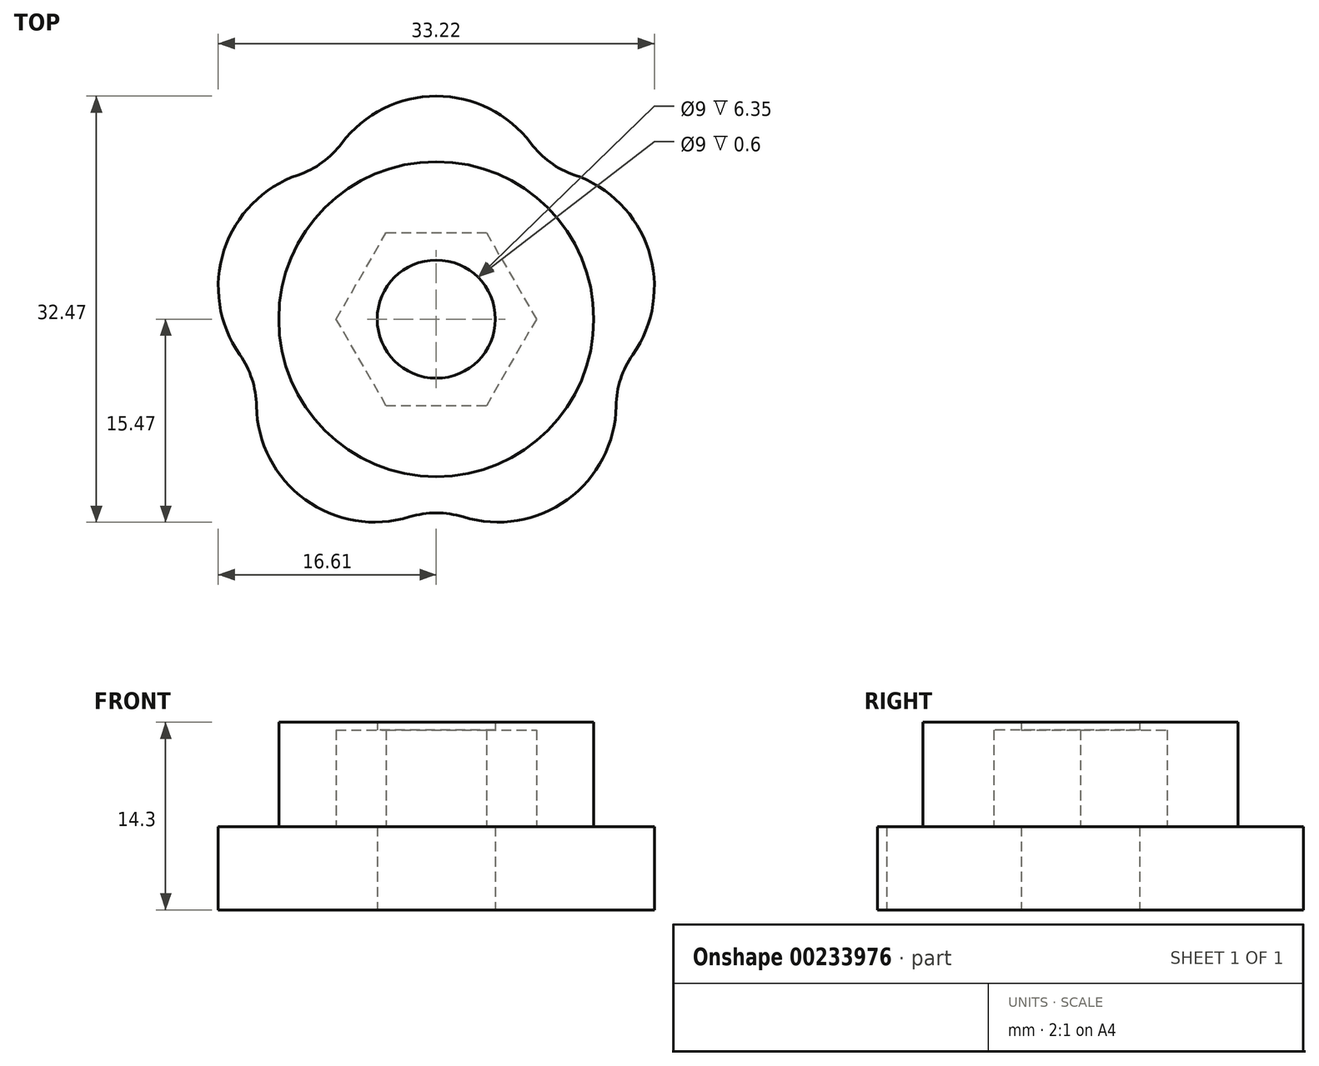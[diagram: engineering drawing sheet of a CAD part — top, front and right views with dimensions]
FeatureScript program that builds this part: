
annotation { "Feature Type Name" : "Feature", "Feature Type Description" : "" }
export const myFeature = defineFeature(function(context is Context, id is Id, definition is map)
    precondition{}
    {
        {
            var Q0;
            Q0=qCreatedBy(makeId("Top.planeOp"),FACE);
            var sketch = newSketch(context, id + "F0", { "sketchPlane" : qUnion([Q0])});
            skCircle(sketch, "E0", {"center": v(0, 0) * mm, "radius": 4.5 * mm});
            skArc(sketch, "E1", {"start": v(7.2, 13.4) * mm, "mid": v(0, 17) * mm, "end": v(-7.2, 13.4) * mm});
            skCircle(sketch, "E2", {"center": v(0, 0) * mm, "radius": 17 * mm, "construction": true});
            skArc(sketch, "E3.1.0", {"start": v(-10.53, 10.99) * mm, "mid": v(-16.17, 5.25) * mm, "end": v(-14.97, -2.7) * mm});
            skArc(sketch, "E3.2.0", {"start": v(-13.7, -6.61) * mm, "mid": v(-10, -13.75) * mm, "end": v(-2.06, -15.07) * mm});
            skArc(sketch, "E3.3.0", {"start": v(2.06, -15.07) * mm, "mid": v(10, -13.75) * mm, "end": v(13.7, -6.61) * mm});
            skArc(sketch, "E3.4.0", {"start": v(14.97, -2.7) * mm, "mid": v(16.17, 5.25) * mm, "end": v(10.53, 10.99) * mm});
            skLineSegment(sketch, "E4", {"start": v(0, 0) * mm, "end": v(-10, 13.75) * mm, "construction": true});
            skArc(sketch, "E5", {"start": v(-10.53, 10.99) * mm, "mid": v(-8.68, 11.95) * mm, "end": v(-7.2, 13.4) * mm});
            skArc(sketch, "E6.1.0", {"start": v(-13.7, -6.61) * mm, "mid": v(-14.04, -4.56) * mm, "end": v(-14.97, -2.7) * mm});
            skArc(sketch, "E6.2.0", {"start": v(2.06, -15.07) * mm, "mid": v(0, -14.77) * mm, "end": v(-2.06, -15.07) * mm});
            skArc(sketch, "E6.3.0", {"start": v(14.97, -2.7) * mm, "mid": v(14.04, -4.56) * mm, "end": v(13.7, -6.61) * mm});
            skArc(sketch, "E6.4.0", {"start": v(7.2, 13.4) * mm, "mid": v(8.68, 11.95) * mm, "end": v(10.53, 10.99) * mm});
            skSolve(sketch);
        }
        {
            var Q0;
            Q0=makeQuery(id+"F0.imprint","IMPRINT",FACE,{"disambiguationData":[TD([[makeQuery(id+"F0.imprint","IMPRINT",EDGE,{"derivedFrom":sQuery(id+"F0.wireOp",EDGE,"E0")}),-1.0]])]});
            extrude(context, id + "F1", {"entities" : qUnion([Q0]), "depth" : 6.35 * mm});
        }
        {
            var Q0;
            Q0=makeQuery(id+"F1.opExtrude","CAP_FACE",FACE,{"disambiguationData":[OSD([sQuery(id+"F0.wireOp",EDGE,"E0"),sQuery(id+"F0.wireOp",EDGE,"E1"),sQuery(id+"F0.wireOp",EDGE,"E3.1.0"),sQuery(id+"F0.wireOp",EDGE,"E3.2.0"),sQuery(id+"F0.wireOp",EDGE,"E3.3.0"),sQuery(id+"F0.wireOp",EDGE,"E3.4.0"),sQuery(id+"F0.wireOp",EDGE,"E5"),sQuery(id+"F0.wireOp",EDGE,"E6.1.0"),sQuery(id+"F0.wireOp",EDGE,"E6.2.0"),sQuery(id+"F0.wireOp",EDGE,"E6.3.0"),sQuery(id+"F0.wireOp",EDGE,"E6.4.0")])],"isStart":false});
            var sketch = newSketch(context, id + "F2", { "sketchPlane" : qUnion([Q0])});
            skCircle(sketch, "E7", {"center": v(0, 0) * mm, "radius": 12 * mm});
            skCircle(sketch, "E8.cCircle", {"center": v(0, 0) * mm, "radius": 6.6 * mm, "construction": true});
            skLineSegment(sketch, "E8.0", {"start": v(-3.81, 6.6) * mm, "end": v(3.81, 6.6) * mm});
            skLineSegment(sketch, "E8.1", {"start": v(3.81, 6.6) * mm, "end": v(7.62, 0) * mm});
            skLineSegment(sketch, "E8.2", {"start": v(7.62, 0) * mm, "end": v(3.81, -6.6) * mm});
            skLineSegment(sketch, "E8.3", {"start": v(3.81, -6.6) * mm, "end": v(-3.81, -6.6) * mm});
            skLineSegment(sketch, "E8.4", {"start": v(-3.81, -6.6) * mm, "end": v(-7.62, 0) * mm});
            skLineSegment(sketch, "E8.5", {"start": v(-7.62, 0) * mm, "end": v(-3.81, 6.6) * mm});
            skPoint(sketch, "E8.0.midPoint", {"position": v(0, 6.6) * mm});
            skSolve(sketch);
        }
        {
            var Q0;
            Q0=makeQuery(id+"F2.imprint","IMPRINT",FACE,{"disambiguationData":[TD([[makeQuery(id+"F2.imprint","IMPRINT",EDGE,{"derivedFrom":sQuery(id+"F2.wireOp",EDGE,"E8.0")}),1.0]])]});
            extrude(context, id + "F3", {"entities" : qUnion([Q0]), "operationType" : NewBodyOperationType.ADD, "depth" : 7.35 * mm});
        }
        {
            var Q0;
            Q0=makeQuery(id+"F3.opExtrude","CAP_FACE",FACE,{"disambiguationData":[OSD([sQuery(id+"F2.wireOp",EDGE,"E7"),sQuery(id+"F2.wireOp",EDGE,"E8.0"),sQuery(id+"F2.wireOp",EDGE,"E8.1"),sQuery(id+"F2.wireOp",EDGE,"E8.2"),sQuery(id+"F2.wireOp",EDGE,"E8.3"),sQuery(id+"F2.wireOp",EDGE,"E8.4"),sQuery(id+"F2.wireOp",EDGE,"E8.5")])],"isStart":false});
            var sketch = newSketch(context, id + "F4", { "sketchPlane" : qUnion([Q0])});
            skCircle(sketch, "E9", {"center": v(0, 0) * mm, "radius": 12 * mm});
            skPoint(sketch, "E9.first.point", {"position": v(-10.47, 5.86) * mm});
            skPoint(sketch, "E9.second.point", {"position": v(11.4, 3.78) * mm});
            skPoint(sketch, "E9.third.point", {"position": v(0.46, -12) * mm});
            skSolve(sketch);
        }
        {
            var Q0;
            Q0 = qSketchRegion(id + "F4", true);
            extrude(context, id + "F5", {"entities" : qUnion([Q0]), "operationType" : NewBodyOperationType.ADD, "depth" : 0.6 * mm});
        }
        {
            var Q0;
            Q0=makeQuery(id+"F1.opExtrude","CAP_FACE",FACE,{"disambiguationData":[OSD([sQuery(id+"F0.wireOp",EDGE,"E0"),sQuery(id+"F0.wireOp",EDGE,"E1"),sQuery(id+"F0.wireOp",EDGE,"E3.1.0"),sQuery(id+"F0.wireOp",EDGE,"E3.2.0"),sQuery(id+"F0.wireOp",EDGE,"E3.3.0"),sQuery(id+"F0.wireOp",EDGE,"E3.4.0"),sQuery(id+"F0.wireOp",EDGE,"E5"),sQuery(id+"F0.wireOp",EDGE,"E6.1.0"),sQuery(id+"F0.wireOp",EDGE,"E6.2.0"),sQuery(id+"F0.wireOp",EDGE,"E6.3.0"),sQuery(id+"F0.wireOp",EDGE,"E6.4.0")])],"isStart":true});
            var sketch = newSketch(context, id + "F6", { "sketchPlane" : qUnion([Q0])});
            skSolve(sketch);
        }
        {
            var Q0;
            Q0=makeQuery(id+"F6.imprint","IMPRINT",FACE,{"disambiguationData":[TD([[makeQuery(id+"F6.imprint","IMPRINT",EDGE,{"derivedFrom":makeQuery(id+"F1.opExtrude","CAP_EDGE",EDGE,{"disambiguationData":[OSD([sQuery(id+"F0.wireOp",EDGE,"E0")])],"isStart":true})}),-1.0]])]});
            extrude(context, id + "F7", {"entities" : qUnion([Q0]), "operationType" : NewBodyOperationType.REMOVE, "oppositeDirection" : true, "depth" : 29.4 * mm});
        }
    });
